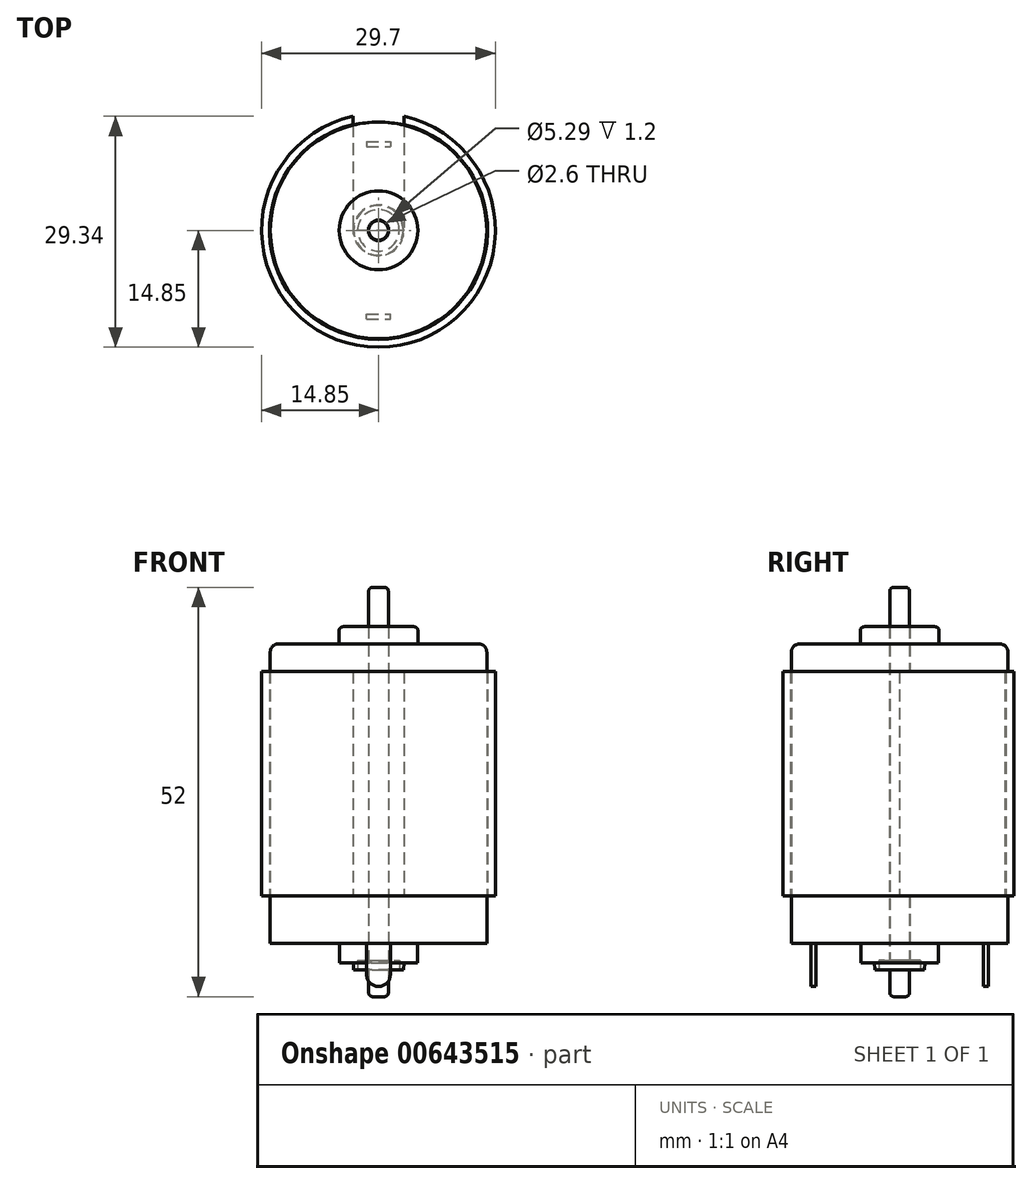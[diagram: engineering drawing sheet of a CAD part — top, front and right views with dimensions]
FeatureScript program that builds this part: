
annotation { "Feature Type Name" : "Feature", "Feature Type Description" : "" }
export const myFeature = defineFeature(function(context is Context, id is Id, definition is map)
    precondition{}
    {
        {
            var Q0;
            Q0=qCreatedBy(makeId("Top.planeOp"),FACE);
            var sketch = newSketch(context, id + "F0", { "sketchPlane" : qUnion([Q0])});
            skCircle(sketch, "E0", {"center": v(0, 0) * mm, "radius": 13.75 * mm});
            skSolve(sketch);
        }
        {
            var Q0;
            Q0=makeQuery(id+"F0.imprint","IMPRINT",FACE,{"disambiguationData":[TD([[makeQuery(id+"F0.imprint","IMPRINT",EDGE,{"derivedFrom":sQuery(id+"F0.wireOp",EDGE,"E0")}),1.0]])]});
            extrude(context, id + "F1", {"entities" : qUnion([Q0]), "depth" : 38 * mm, "offsetDistance" : 25 * mm});
        }
        {
            var Q0;
            Q0=makeQuery(id+"F1.opExtrude","CAP_FACE",FACE,{"disambiguationData":[OSD([sQuery(id+"F0.wireOp",EDGE,"E0")])],"isStart":false});
            var sketch = newSketch(context, id + "F2", { "sketchPlane" : qUnion([Q0])});
            skCircle(sketch, "E1", {"center": v(0, 0) * mm, "radius": 5 * mm});
            skSolve(sketch);
        }
        {
            var Q0;
            Q0 = qSketchRegion(id + "F2", true);
            extrude(context, id + "F3", {"entities" : qUnion([Q0]), "operationType" : NewBodyOperationType.ADD, "depth" : 2.2 * mm, "offsetDistance" : 25 * mm});
        }
        {
            var Q0;
            Q0=makeQuery(id+"F1.opExtrude","CAP_EDGE",EDGE,{"disambiguationData":[OSD([sQuery(id+"F0.wireOp",EDGE,"E0")])],"isStart":false});
            fillet(context, id + "F4", {"entities" : qUnion([Q0]), "radius" : 1 * mm, "tangentPropagation" : true, "allowEdgeOverflow" : false});
        }
        {
            var Q0;
            Q0=makeQuery(id+"F3.opExtrude","CAP_EDGE",EDGE,{"disambiguationData":[OSD([sQuery(id+"F2.wireOp",EDGE,"E1")])],"isStart":false});
            fillet(context, id + "F5", {"entities" : qUnion([Q0]), "radius" : .5 * mm, "tangentPropagation" : true, "allowEdgeOverflow" : false});
        }
        {
            var Q0;
            Q0=makeQuery(id+"F1.opExtrude","CAP_FACE",FACE,{"disambiguationData":[OSD([sQuery(id+"F0.wireOp",EDGE,"E0")])],"isStart":true});
            var sketch = newSketch(context, id + "F6", { "sketchPlane" : qUnion([Q0])});
            skCircle(sketch, "E2", {"center": v(0, 0) * mm, "radius": 4.95 * mm});
            skSolve(sketch);
        }
        {
            var Q0;
            Q0=makeQuery(id+"F6.imprint","IMPRINT",FACE,{"disambiguationData":[TD([[makeQuery(id+"F6.imprint","IMPRINT",EDGE,{"derivedFrom":sQuery(id+"F6.wireOp",EDGE,"E2")}),1.0]])]});
            extrude(context, id + "F7", {"entities" : qUnion([Q0]), "operationType" : NewBodyOperationType.ADD, "depth" : 2.5 * mm, "offsetDistance" : 25 * mm});
        }
        {
            var Q0;
            Q0=makeQuery(id+"F7.opExtrude","CAP_FACE",FACE,{"disambiguationData":[OSD([sQuery(id+"F6.wireOp",EDGE,"E2")])],"isStart":false});
            var sketch = newSketch(context, id + "F8", { "sketchPlane" : qUnion([Q0])});
            skCircle(sketch, "E3", {"center": v(0, 0) * mm, "radius": 3.22 * mm});
            skSolve(sketch);
        }
        {
            var Q0;
            Q0=makeQuery(id+"F8.imprint","IMPRINT",FACE,{"disambiguationData":[TD([[makeQuery(id+"F8.imprint","IMPRINT",EDGE,{"derivedFrom":sQuery(id+"F8.wireOp",EDGE,"E3")}),1.0]])]});
            extrude(context, id + "F9", {"entities" : qUnion([Q0]), "operationType" : NewBodyOperationType.ADD, "depth" : .9 * mm, "offsetDistance" : 25 * mm, "hasDraft" : true, "draftAngle" : 5 * degree, "draftPullDirection" : true});
        }
        {
            var Q0;
            Q0=makeQuery(id+"F9.opExtrude","CAP_FACE",FACE,{"disambiguationData":[OSD([sQuery(id+"F8.wireOp",EDGE,"E3")])],"isStart":false});
            var sketch = newSketch(context, id + "F10", { "sketchPlane" : qUnion([Q0])});
            skCircle(sketch, "E4", {"center": v(0, 0) * mm, "radius": 2.65 * mm});
            skSolve(sketch);
        }
        {
            var Q0;
            Q0=makeQuery(id+"F10.imprint","IMPRINT",FACE,{"disambiguationData":[TD([[makeQuery(id+"F10.imprint","IMPRINT",EDGE,{"derivedFrom":sQuery(id+"F10.wireOp",EDGE,"E4")}),1.0]])]});
            extrude(context, id + "F11", {"entities" : qUnion([Q0]), "operationType" : NewBodyOperationType.REMOVE, "oppositeDirection" : true, "depth" : 1.2 * mm, "offsetDistance" : 25 * mm});
        }
        {
            var Q0;
            Q0=makeQuery(id+"F11.boolean.opBoolean","COPY",FACE,{"derivedFrom":makeQuery(id+"F11.opExtrude","CAP_FACE",FACE,{"disambiguationData":[OSD([sQuery(id+"F10.wireOp",EDGE,"E4")])],"isStart":false})});
            var sketch = newSketch(context, id + "F12", { "sketchPlane" : qUnion([Q0])});
            skCircle(sketch, "E5", {"center": v(0, 0) * mm, "radius": 1.3 * mm});
            skSolve(sketch);
        }
        {
            var Q0;
            Q0=makeQuery(id+"F12.imprint","IMPRINT",FACE,{"disambiguationData":[TD([[makeQuery(id+"F12.imprint","IMPRINT",EDGE,{"derivedFrom":sQuery(id+"F12.wireOp",EDGE,"E5")}),1.0]])]});
            extrude(context, id + "F13", {"entities" : qUnion([Q0]), "operationType" : NewBodyOperationType.REMOVE, "endBound" : BoundingType.THROUGH_ALL, "oppositeDirection" : true, "depth" : 25 * mm, "offsetDistance" : 25 * mm});
        }
        {
            var Q0;
            Q0=makeQuery(id+"F3.opExtrude","CAP_FACE",FACE,{"disambiguationData":[OSD([sQuery(id+"F2.wireOp",EDGE,"E1")])],"isStart":false});
            var sketch = newSketch(context, id + "F14", { "sketchPlane" : qUnion([Q0])});
            skCircle(sketch, "E6", {"center": v(0, 0) * mm, "radius": 1.25 * mm});
            skSolve(sketch);
        }
        {
            var Q0;
            Q0=makeQuery(id+"F14.imprint","IMPRINT",FACE,{"disambiguationData":[TD([[makeQuery(id+"F14.imprint","IMPRINT",EDGE,{"derivedFrom":sQuery(id+"F14.wireOp",EDGE,"E6")}),1.0]])]});
            extrude(context, id + "F15", {"entities" : qUnion([Q0]), "depth" : 5 * mm, "offsetDistance" : 25 * mm, "hasSecondDirection" : true, "secondDirectionOppositeDirection" : true, "secondDirectionDepth" : 47 * mm});
        }
        {
            var Q0;
            Q0=makeQuery(id+"F15.opExtrude","CAP_EDGE",EDGE,{"disambiguationData":[OSD([sQuery(id+"F14.wireOp",EDGE,"E6")])],"isStart":false});
            fillet(context, id + "F16", {"entities" : qUnion([Q0]), "radius" : .5 * mm, "tangentPropagation" : true, "allowEdgeOverflow" : false});
        }
        {
            var Q0;
            Q0=makeQuery(id+"F15.opExtrude","CAP_EDGE",EDGE,{"disambiguationData":[OSD([sQuery(id+"F14.wireOp",EDGE,"E6")])],"isStart":true});
            fillet(context, id + "F17", {"entities" : qUnion([Q0]), "radius" : .5 * mm, "tangentPropagation" : true, "allowEdgeOverflow" : false});
        }
        {
            var Q0;
            Q0=makeQuery(id+"F1.opExtrude","CAP_FACE",FACE,{"disambiguationData":[OSD([sQuery(id+"F0.wireOp",EDGE,"E0")])],"isStart":true});
            var sketch = newSketch(context, id + "F18", { "sketchPlane" : qUnion([Q0])});
            skLineSegment(sketch, "E7", {"start": v(-13.75, 0) * mm, "end": v(13.75, 0) * mm, "construction": true});
            skLineSegment(sketch, "E8", {"start": v(0, -13.75) * mm, "end": v(0, 13.75) * mm, "construction": true});
            skLineSegment(sketch, "E9.bottom", {"start": v(-1.5, -11.25) * mm, "end": v(1.5, -11.25) * mm});
            skLineSegment(sketch, "E9.top", {"start": v(-1.5, -10.65) * mm, "end": v(1.5, -10.65) * mm});
            skLineSegment(sketch, "E9.left", {"start": v(-1.5, -11.25) * mm, "end": v(-1.5, -10.65) * mm});
            skLineSegment(sketch, "E9.right", {"start": v(1.5, -11.25) * mm, "end": v(1.5, -10.65) * mm});
            skLineSegment(sketch, "E10.MirrorCS", {"start": v(-1.5, 11.25) * mm, "end": v(1.5, 11.25) * mm});
            skLineSegment(sketch, "E11.MirrorCS", {"start": v(-1.5, 10.65) * mm, "end": v(1.5, 10.65) * mm});
            skLineSegment(sketch, "E12.MirrorCS", {"start": v(1.5, 11.25) * mm, "end": v(1.5, 10.65) * mm});
            skLineSegment(sketch, "E13.MirrorCS", {"start": v(-1.5, 11.25) * mm, "end": v(-1.5, 10.65) * mm});
            skSolve(sketch);
        }
        {
            var Q0;
            Q0 = qSketchRegion(id + "F18", true);
            extrude(context, id + "F19", {"entities" : qUnion([Q0]), "operationType" : NewBodyOperationType.ADD, "depth" : 5.5 * mm, "offsetDistance" : 25 * mm});
        }
        {
            var Q0;
            Q0=makeQuery(id+"F19.opExtrude","CAP_EDGE",EDGE,{"disambiguationData":[OSD([sQuery(id+"F18.wireOp",EDGE,"E9.right")])],"isStart":false});
            var Q1;
            Q1=makeQuery(id+"F19.opExtrude","CAP_EDGE",EDGE,{"disambiguationData":[OSD([sQuery(id+"F18.wireOp",EDGE,"E9.left")])],"isStart":false});
            var Q2;
            Q2=makeQuery(id+"F19.opExtrude","CAP_EDGE",EDGE,{"disambiguationData":[OSD([sQuery(id+"F18.wireOp",EDGE,"E12.MirrorCS")])],"isStart":false});
            var Q3;
            Q3=makeQuery(id+"F19.opExtrude","CAP_EDGE",EDGE,{"disambiguationData":[OSD([sQuery(id+"F18.wireOp",EDGE,"E13.MirrorCS")])],"isStart":false});
            fillet(context, id + "F20", {"entities" : qUnion([Q0, Q1, Q2, Q3]), "radius" : 1.5 * mm, "tangentPropagation" : true, "allowEdgeOverflow" : false});
        }
        {
            var Q0;
            Q0=qCreatedBy(makeId("Top.planeOp"),FACE);
            var sketch = newSketch(context, id + "F21", { "sketchPlane" : qUnion([Q0])});
            skCircle(sketch, "E14", {"center": v(0, 0) * mm, "radius": 13.85 * mm});
            skCircle(sketch, "E15.0", {"center": v(0, 0) * mm, "radius": 14.85 * mm});
            skSolve(sketch);
        }
        {
            var Q0;
            Q0=makeQuery(id+"F21.imprint","IMPRINT",FACE,{"disambiguationData":[TD([[makeQuery(id+"F21.imprint","IMPRINT",EDGE,{"derivedFrom":sQuery(id+"F21.wireOp",EDGE,"E14")}),-1.0]])]});
            extrude(context, id + "F22", {"entities" : qUnion([Q0]), "depth" : 34.5 * mm, "offsetDistance" : 25 * mm});
        }
        {
            var Q0;
            Q0=makeQuery(id+"F22.opExtrude","CAP_FACE",FACE,{"disambiguationData":[OSD([sQuery(id+"F21.wireOp",EDGE,"E14"),sQuery(id+"F21.wireOp",EDGE,"E15.0")])],"isStart":true});
            extrude(context, id + "F23", {"entities" : qUnion([Q0]), "operationType" : NewBodyOperationType.REMOVE, "oppositeDirection" : true, "depth" : 6 * mm, "offsetDistance" : 25 * mm});
        }
        {
            var Q0;
            Q0=qCreatedBy(makeId("Front.planeOp"),FACE);
            var sketch = newSketch(context, id + "F24", { "sketchPlane" : qUnion([Q0])});
            skLineSegment(sketch, "E16", {"start": v(0, 49.48) * mm, "end": v(0, -18.9) * mm, "construction": true});
            skLineSegment(sketch, "E17.0", {"start": v(-3.25, 34.5) * mm, "end": v(-3.25, 6) * mm});
            skLineSegment(sketch, "E18.0", {"start": v(3.25, 34.5) * mm, "end": v(3.25, 6) * mm});
            skLineSegment(sketch, "E19", {"start": v(3.25, 34.5) * mm, "end": v(-3.25, 34.5) * mm});
            skLineSegment(sketch, "E20", {"start": v(3.25, 6) * mm, "end": v(-3.25, 6) * mm});
            skSolve(sketch);
        }
        {
            var Q0;
            Q0 = qSketchRegion(id + "F24", true);
            extrude(context, id + "F25", {"entities" : qUnion([Q0]), "operationType" : NewBodyOperationType.REMOVE, "oppositeDirection" : true, "depth" : 25 * mm, "offsetDistance" : 25 * mm});
        }
    });
